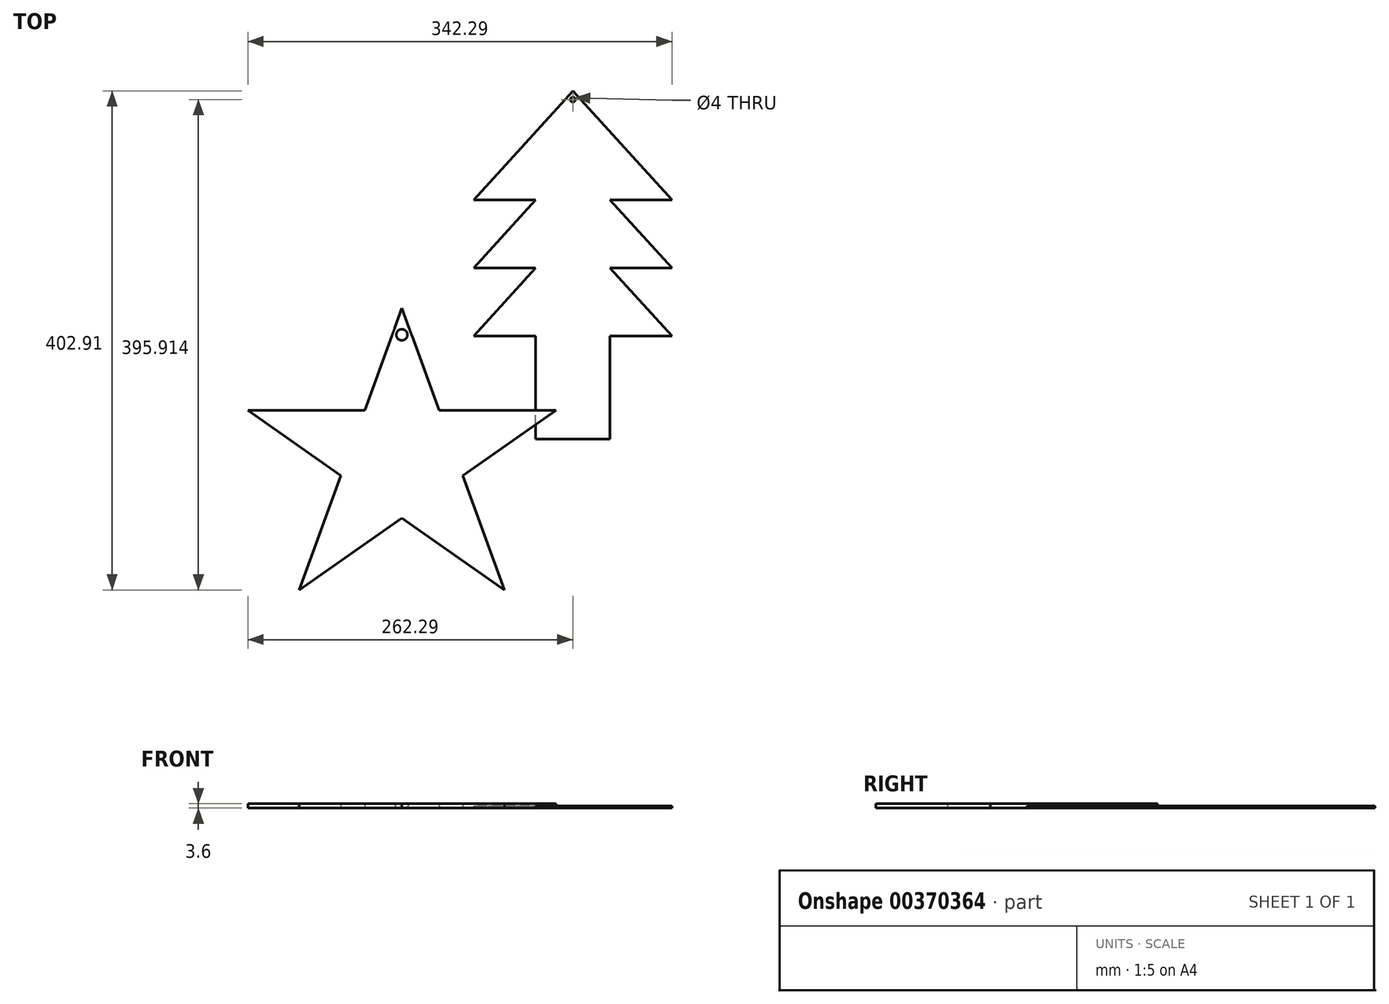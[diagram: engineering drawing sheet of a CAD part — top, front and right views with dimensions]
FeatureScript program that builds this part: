
annotation { "Feature Type Name" : "Feature", "Feature Type Description" : "" }
export const myFeature = defineFeature(function(context is Context, id is Id, definition is map)
    precondition{}
    {
        {
            var Q0;
            Q0=qCreatedBy(makeId("Top.planeOp"),FACE);
            var sketch = newSketch(context, id + "F0", { "sketchPlane" : qUnion([Q0])});
            skLineSegment(sketch, "E0", {"start": v(0, 175.01) * mm, "end": v(0, -124.99) * mm, "construction": true});
            skLineSegment(sketch, "E1", {"start": v(-80, 66.72) * mm, "end": v(-30, 66.72) * mm});
            skLineSegment(sketch, "E2.1.0.0", {"start": v(-80, 11.72) * mm, "end": v(-30, 11.72) * mm});
            skLineSegment(sketch, "E2.2.0.0", {"start": v(-80, -43.28) * mm, "end": v(-30, -43.28) * mm});
            skLineSegment(sketch, "E2.direction1", {"start": v(-80, 66.72) * mm, "end": v(-80, 11.72) * mm, "construction": true});
            skLineSegment(sketch, "E3.left", {"start": v(-30, -43.4) * mm, "end": v(-30, -43.28) * mm});
            skLineSegment(sketch, "E4.trimOffspring", {"start": v(-30, 66.72) * mm, "end": v(-80, 11.72) * mm});
            skLineSegment(sketch, "E5.trimOffspring", {"start": v(-30, 11.72) * mm, "end": v(-80, -43.28) * mm});
            skLineSegment(sketch, "E6", {"start": v(-30, -43.4) * mm, "end": v(-30, -126.25) * mm});
            skLineSegment(sketch, "E7", {"start": v(-30, -126.25) * mm, "end": v(0, -126.25) * mm});
            skLineSegment(sketch, "E8", {"start": v(0, 154.72) * mm, "end": v(-80, 66.72) * mm});
            skLineSegment(sketch, "E9.MirrorCS", {"start": v(30, -43.4) * mm, "end": v(30, -43.28) * mm});
            skLineSegment(sketch, "E10.MirrorCS", {"start": v(80, -43.28) * mm, "end": v(30, -43.28) * mm});
            skLineSegment(sketch, "E11.MirrorCS", {"start": v(80, 11.72) * mm, "end": v(30, 11.72) * mm});
            skLineSegment(sketch, "E12.MirrorCS", {"start": v(30, 66.72) * mm, "end": v(80, 11.72) * mm});
            skLineSegment(sketch, "E13.MirrorCS", {"start": v(30, 11.72) * mm, "end": v(80, -43.28) * mm});
            skLineSegment(sketch, "E14.MirrorCS", {"start": v(30, -43.4) * mm, "end": v(30, -126.25) * mm});
            skLineSegment(sketch, "E15.MirrorCS", {"start": v(80, 66.72) * mm, "end": v(30, 66.72) * mm});
            skLineSegment(sketch, "E16.MirrorCS", {"start": v(80, 66.72) * mm, "end": v(80, 11.72) * mm, "construction": true});
            skLineSegment(sketch, "E17.MirrorCS", {"start": v(0, 154.72) * mm, "end": v(80, 66.72) * mm});
            skLineSegment(sketch, "E18.MirrorCS", {"start": v(30, -126.25) * mm, "end": v(0, -126.25) * mm});
            skCircle(sketch, "E19", {"center": v(0, 147.72) * mm, "radius": 2 * mm});
            skSolve(sketch);
        }
        {
            var Q0;
            Q0 = qSketchRegion(id + "F0", true);
            extrude(context, id + "F1", {"entities" : qUnion([Q0]), "depth" : 1.6 * mm});
        }
        {
            var Q0;
            Q0=makeQuery(id+"F0.imprint","IMPRINT",FACE,{"disambiguationData":[TD([[makeQuery(id+"F0.imprint","IMPRINT",EDGE,{"derivedFrom":sQuery(id+"F0.wireOp",EDGE,"E19")}),1.0]])]});
            extrude(context, id + "F2", {"entities" : qUnion([Q0]), "operationType" : NewBodyOperationType.REMOVE, "endBound" : BoundingType.THROUGH_ALL, "oppositeDirection" : true, "depth" : 25 * mm});
        }
        {
            var Q0;
            Q0=qCreatedBy(makeId("Top.planeOp"),FACE);
            var sketch = newSketch(context, id + "F3", { "sketchPlane" : qUnion([Q0])});
            skLineSegment(sketch, "E20", {"start": v(0, -12.6) * mm, "end": v(0, -60.38) * mm, "construction": true});
            skLineSegment(sketch, "E21", {"start": v(0, -20.78) * mm, "end": v(-5, -34.52) * mm});
            skLineSegment(sketch, "E22", {"start": v(-13.8, -58.68) * mm, "end": v(0, -49.02) * mm});
            skLineSegment(sketch, "E23", {"start": v(-20.71, -34.52) * mm, "end": v(-8.2, -43.29) * mm});
            skPoint(sketch, "E24", {"position": v(-8.2, -43.29) * mm});
            skPoint(sketch, "E25", {"position": v(-5, -34.52) * mm});
            skLineSegment(sketch, "E26.trimOffspring", {"start": v(-5, -34.52) * mm, "end": v(-20.71, -34.52) * mm});
            skLineSegment(sketch, "E27.trimOffspring", {"start": v(-8.2, -43.29) * mm, "end": v(-13.8, -58.68) * mm});
            skCircle(sketch, "E28", {"center": v(0, -24.35) * mm, "radius": 0.75 * mm});
            skLineSegment(sketch, "E29.MirrorCS", {"start": v(0, -20.78) * mm, "end": v(5, -34.52) * mm});
            skLineSegment(sketch, "E30.MirrorCS", {"start": v(5, -34.52) * mm, "end": v(20.71, -34.52) * mm});
            skLineSegment(sketch, "E31.MirrorCS", {"start": v(20.71, -34.52) * mm, "end": v(8.2, -43.29) * mm});
            skLineSegment(sketch, "E32.MirrorCS", {"start": v(8.2, -43.29) * mm, "end": v(13.8, -58.68) * mm});
            skLineSegment(sketch, "E33.MirrorCS", {"start": v(13.8, -58.68) * mm, "end": v(0, -49.02) * mm});
            skSolve(sketch);
        }
        {
            var Q0;
            Q0 = qSketchRegion(id + "F3", true);
            extrude(context, id + "F4", {"entities" : qUnion([Q0]), "depth" : 0.6 * mm});
        }
        {
            var Q0;
            Q0 = qSketchRegion(id + "F3", true);
            extrude(context, id + "F5", {"entities" : qUnion([Q0]), "operationType" : NewBodyOperationType.REMOVE, "endBound" : BoundingType.THROUGH_ALL, "oppositeDirection" : true, "depth" : 25 * mm});
        }
        {
            var Q0;
            Q0=makeQuery(id+"F4.opExtrude","CAP_EDGE",EDGE,{"disambiguationData":[OSD([sQuery(id+"F3.wireOp",EDGE,"E28")])],"isStart":false});
            var Q1;
            Q1=makeQuery(id+"F1.opExtrude","CAP_EDGE",EDGE,{"disambiguationData":[OSD([sQuery(id+"F0.wireOp",EDGE,"kLHDiUT2-VZ1F-veUs-UEKf-4xIFSOdoPKTw")])],"isStart":false});
            var Q2;
            Q2=makeQuery(id+"F1.opExtrude","CAP_EDGE",EDGE,{"disambiguationData":[OSD([sQuery(id+"F0.wireOp",EDGE,"E19")])],"isStart":false});
            fillet(context, id + "F6", {"entities" : qUnion([Q0, Q1, Q2]), "radius" : 0.6 * mm, "tangentPropagation" : true, "allowEdgeOverflow" : false});
        }
        {
            var Q0;
            Q0=makeQuery(id+"F1.opExtrude","SWEPT_BODY",BODY,{"disambiguationData":[OSD([sQuery(id+"F0.wireOp",EDGE,"E1"),sQuery(id+"F0.wireOp",EDGE,"E2.1.0.0"),sQuery(id+"F0.wireOp",EDGE,"E2.2.0.0"),sQuery(id+"F0.wireOp",EDGE,"E3.left"),sQuery(id+"F0.wireOp",EDGE,"E4.trimOffspring"),sQuery(id+"F0.wireOp",EDGE,"E5.trimOffspring"),sQuery(id+"F0.wireOp",EDGE,"E6"),sQuery(id+"F0.wireOp",EDGE,"E7"),sQuery(id+"F0.wireOp",EDGE,"E8"),sQuery(id+"F0.wireOp",EDGE,"E9.MirrorCS"),sQuery(id+"F0.wireOp",EDGE,"E10.MirrorCS"),sQuery(id+"F0.wireOp",EDGE,"E11.MirrorCS"),sQuery(id+"F0.wireOp",EDGE,"E12.MirrorCS"),sQuery(id+"F0.wireOp",EDGE,"E13.MirrorCS"),sQuery(id+"F0.wireOp",EDGE,"E14.MirrorCS"),sQuery(id+"F0.wireOp",EDGE,"E15.MirrorCS"),sQuery(id+"F0.wireOp",EDGE,"E17.MirrorCS"),sQuery(id+"F0.wireOp",EDGE,"E18.MirrorCS"),sQuery(id+"F0.wireOp",EDGE,"E19")])]});
            var Q1;
            Q1=makeQuery(id+"F1.opExtrude","CAP_EDGE",EDGE,{"disambiguationData":[OSD([sQuery(id+"F0.wireOp",EDGE,"E7"),sQuery(id+"F0.wireOp",EDGE,"E18.MirrorCS")])],"isStart":false});
            transform(context, id + "F7", {"entities" : qUnion([Q0]), "transformType" : TransformType.TRANSLATION_3D, "dx" : 138 * mm, "dy" : 0 * mm, "dz" : 0 * mm, "makeCopy" : false});
        }
        {
            var Q0;
            Q0=makeQuery(id+"F4.opExtrude","SWEPT_BODY",BODY,{"disambiguationData":[OSD([sQuery(id+"F3.wireOp",EDGE,"E21"),sQuery(id+"F3.wireOp",EDGE,"E22"),sQuery(id+"F3.wireOp",EDGE,"E23"),sQuery(id+"F3.wireOp",EDGE,"E26.trimOffspring"),sQuery(id+"F3.wireOp",EDGE,"E27.trimOffspring"),sQuery(id+"F3.wireOp",EDGE,"E28"),sQuery(id+"F3.wireOp",EDGE,"E29.MirrorCS"),sQuery(id+"F3.wireOp",EDGE,"E30.MirrorCS"),sQuery(id+"F3.wireOp",EDGE,"E31.MirrorCS"),sQuery(id+"F3.wireOp",EDGE,"E32.MirrorCS"),sQuery(id+"F3.wireOp",EDGE,"E33.MirrorCS")])]});
            var Q1;
            Q1=sQuery(id+"F3.wireOp",VERTEX,"E29.MirrorCS.start");
            transform(context, id + "F8", {"entities" : qUnion([Q0]), "transformType" : TransformType.SCALE_UNIFORMLY, "scale" : 6, "scalePoint" : qUnion([Q1]), "makeCopy" : false});
        }
    });
